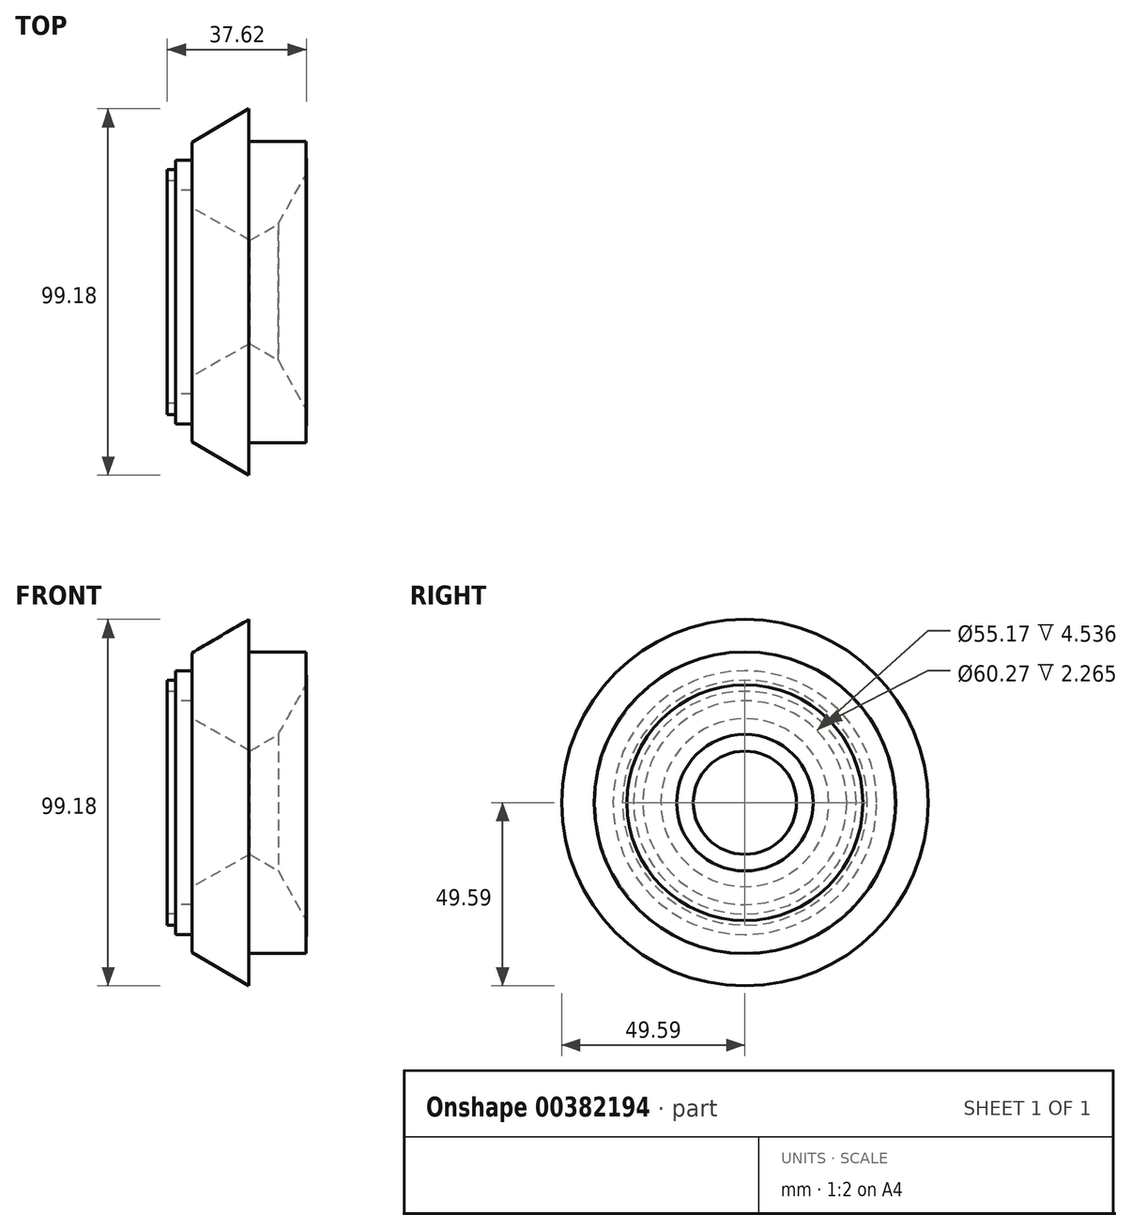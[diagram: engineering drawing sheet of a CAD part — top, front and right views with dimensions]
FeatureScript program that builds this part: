
annotation { "Feature Type Name" : "Feature", "Feature Type Description" : "" }
export const myFeature = defineFeature(function(context is Context, id is Id, definition is map)
    precondition{}
    {
        {
            var Q0;
            Q0=qCreatedBy(makeId("Front.planeOp"),FACE);
            var sketch = newSketch(context, id + "F0", { "sketchPlane" : qUnion([Q0])});
            skLineSegment(sketch, "E0", {"start": v(-58.45, 0) * mm, "end": v(59.36, 0) * mm, "construction": true});
            skCircle(sketch, "E1.cCircle", {"center": v(-30.23, 31.77) * mm, "radius": 15.43 * mm, "construction": true});
            skLineSegment(sketch, "E1.1", {"start": v(-30.07, 13.96) * mm, "end": v(-45.57, 22.73) * mm});
            skLineSegment(sketch, "E1.2", {"start": v(-45.57, 22.73) * mm, "end": v(-45.73, 40.54) * mm});
            skLineSegment(sketch, "E1.3", {"start": v(-45.73, 40.54) * mm, "end": v(-30.38, 49.59) * mm});
            skPoint(sketch, "E1.0.midPoint", {"position": v(-22.4, 18.48) * mm});
            skPoint(sketch, "E2.oppositeSnap0", {"position": v(-45.65, 31.64) * mm});
            skLineSegment(sketch, "E2.left", {"start": v(-45.65, 31.64) * mm, "end": v(-45.65, 31.64) * mm});
            skLineSegment(sketch, "E3.bottom", {"start": v(-41.15, 27.59) * mm, "end": v(-50.15, 27.59) * mm});
            skLineSegment(sketch, "E3.top", {"start": v(-41.15, 35.7) * mm, "end": v(-50.15, 35.7) * mm});
            skLineSegment(sketch, "E3.left", {"start": v(-41.15, 27.59) * mm, "end": v(-41.15, 35.7) * mm});
            skLineSegment(sketch, "E3.right", {"start": v(-50.15, 27.59) * mm, "end": v(-50.15, 35.7) * mm});
            skLineSegment(sketch, "E4.bottom", {"start": v(-47.89, 30.13) * mm, "end": v(-52.42, 30.13) * mm});
            skLineSegment(sketch, "E4.top", {"start": v(-47.89, 33.14) * mm, "end": v(-52.42, 33.14) * mm});
            skLineSegment(sketch, "E4.left", {"start": v(-47.89, 30.13) * mm, "end": v(-47.89, 33.14) * mm});
            skLineSegment(sketch, "E4.right", {"start": v(-52.42, 30.13) * mm, "end": v(-52.42, 33.14) * mm});
            skPoint(sketch, "E4.middle", {"position": v(-50.15, 31.64) * mm});
            skPoint(sketch, "E5.cCircle.perimeterSnap0", {"position": v(-22.63, 45.2) * mm});
            skPoint(sketch, "E5.0.startSnap0", {"position": v(-22.63, 45.2) * mm});
            skLineSegment(sketch, "E6.top", {"start": v(-30.38, 40.81) * mm, "end": v(-14.88, 40.81) * mm});
            skLineSegment(sketch, "E6.left", {"start": v(-30.38, 49.59) * mm, "end": v(-30.38, 40.81) * mm});
            skPoint(sketch, "E7.endSnap0", {"position": v(-14.8, 31.9) * mm});
            skLineSegment(sketch, "E8", {"start": v(-30.07, 13.96) * mm, "end": v(-22.4, 18.48) * mm});
            skLineSegment(sketch, "E9", {"start": v(-14.8, 31.9) * mm, "end": v(-14.88, 40.81) * mm});
            skLineSegment(sketch, "E10", {"start": v(-22.4, 18.48) * mm, "end": v(-14.8, 31.9) * mm});
            skSolve(sketch);
        }
        {
            var Q0;
            Q0 = qSketchRegion(id + "F0", true);
            var Q1;
            Q1=sQuery(id+"F0.wireOp",EDGE,"E0");
            revolve(context, id + "F1", {"entities" : qUnion([Q0]), "axis" : qUnion([Q1]), "revolveType" : RevolveType.FULL});
        }
    });
